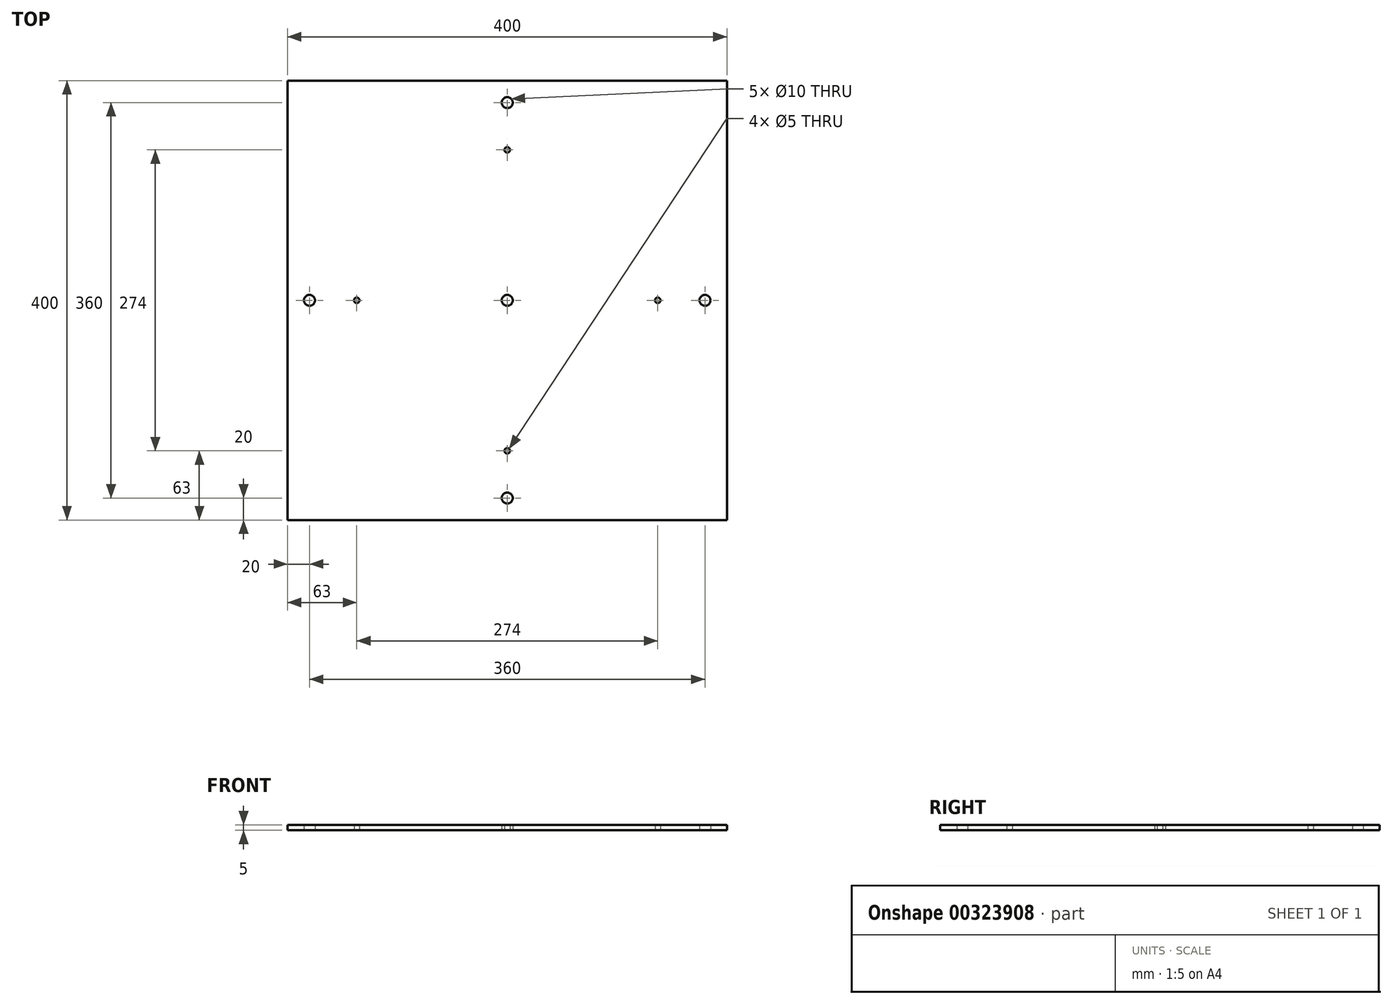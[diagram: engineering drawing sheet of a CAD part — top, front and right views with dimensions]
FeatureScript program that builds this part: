
annotation { "Feature Type Name" : "Feature", "Feature Type Description" : "" }
export const myFeature = defineFeature(function(context is Context, id is Id, definition is map)
    precondition{}
    {
        {
            var Q0;
            Q0=qCreatedBy(makeId("Top.planeOp"),FACE);
            var sketch = newSketch(context, id + "F0", { "sketchPlane" : qUnion([Q0])});
            skLineSegment(sketch, "E0.bottom", {"start": v(-200, 200) * mm, "end": v(200, 200) * mm});
            skLineSegment(sketch, "E0.top", {"start": v(-200, -200) * mm, "end": v(200, -200) * mm});
            skLineSegment(sketch, "E0.right", {"start": v(200, 200) * mm, "end": v(200, -200) * mm});
            skLineSegment(sketch, "E1", {"start": v(-200, 200) * mm, "end": v(-200, -200) * mm});
            skCircle(sketch, "E2", {"center": v(0, 0) * mm, "radius": 5 * mm});
            skCircle(sketch, "E3", {"center": v(-137, 0) * mm, "radius": 2.5 * mm});
            skCircle(sketch, "E4", {"center": v(-180, 0) * mm, "radius": 5 * mm});
            skCircle(sketch, "E5", {"center": v(0, 137) * mm, "radius": 2.5 * mm});
            skCircle(sketch, "E6", {"center": v(0, 180) * mm, "radius": 5 * mm});
            skCircle(sketch, "E7", {"center": v(137, 0) * mm, "radius": 2.5 * mm});
            skCircle(sketch, "E8", {"center": v(0, -137) * mm, "radius": 2.5 * mm});
            skCircle(sketch, "E9", {"center": v(0, -180) * mm, "radius": 5 * mm});
            skCircle(sketch, "E10", {"center": v(180, 0) * mm, "radius": 5 * mm});
            skSolve(sketch);
        }
        {
            var Q0;
            {var subQ3=sQuery(id+"F0.wireOp",EDGE,"E0.bottom");Q0=makeQuery(id+"F0.imprint","IMPRINT",FACE,{"disambiguationData":[TD([[makeQuery(id+"F0.imprint","IMPRINT",EDGE,{"derivedFrom":subQ3}),-1.0]])]});}
            extrude(context, id + "F1", {"entities" : qUnion([Q0]), "depth" : 5 * mm});
        }
    });
